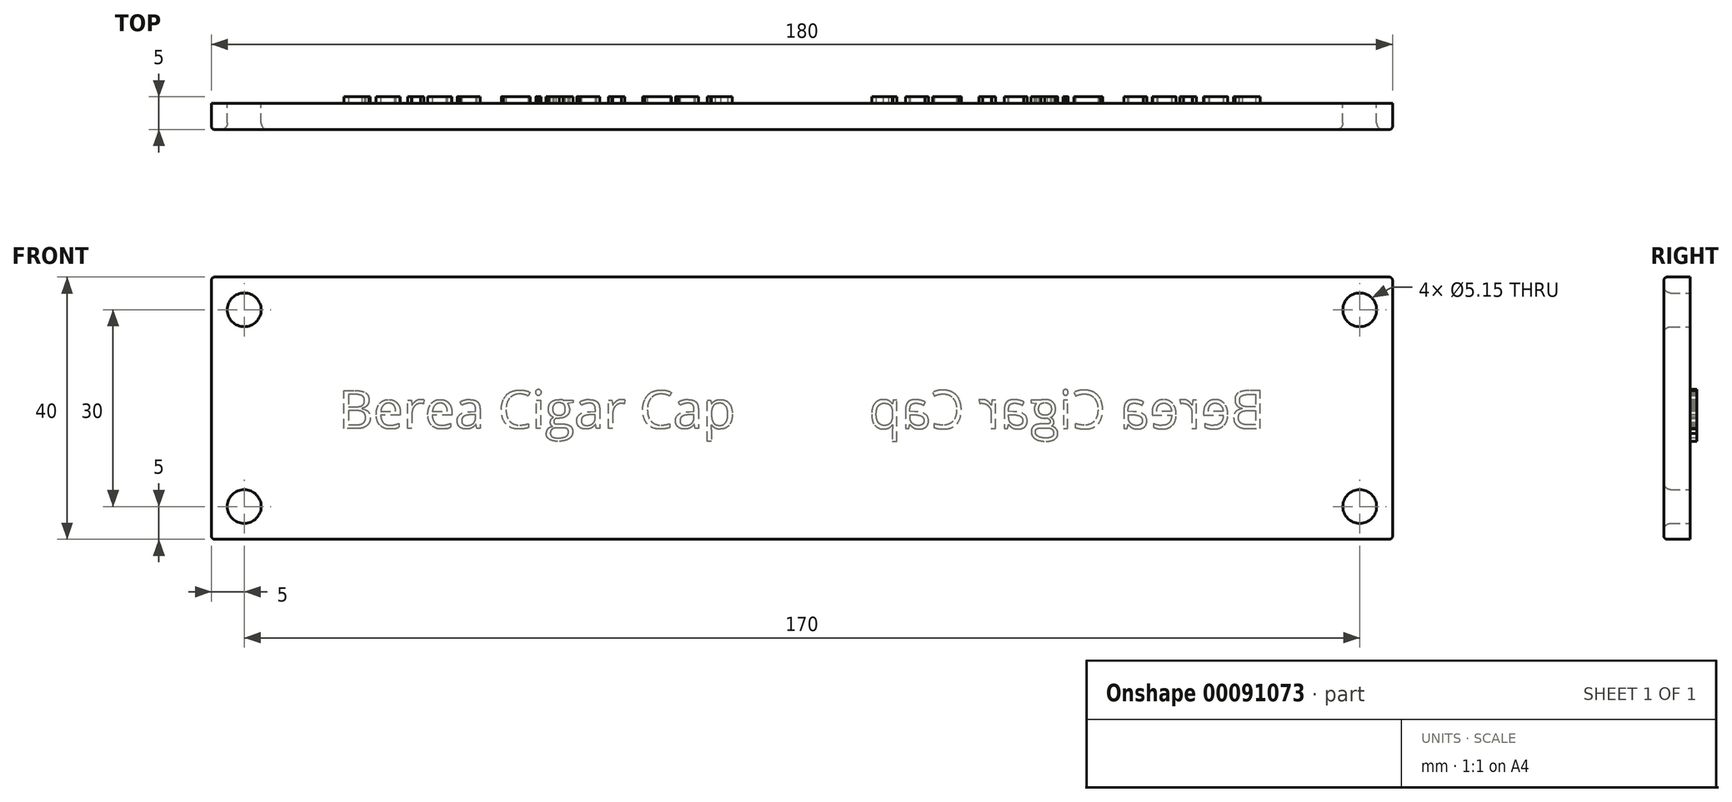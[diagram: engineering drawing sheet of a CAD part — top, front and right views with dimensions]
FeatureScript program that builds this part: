
annotation { "Feature Type Name" : "Feature", "Feature Type Description" : "" }
export const myFeature = defineFeature(function(context is Context, id is Id, definition is map)
    precondition{}
    {
        {
            var Q0;
            Q0=qCreatedBy(makeId("Front.planeOp"),FACE);
            var sketch = newSketch(context, id + "F0", { "sketchPlane" : qUnion([Q0])});
            skLineSegment(sketch, "E0.bottom", {"start": v(-90, -20) * mm, "end": v(90, -20) * mm});
            skLineSegment(sketch, "E0.top", {"start": v(-90, 20) * mm, "end": v(90, 20) * mm});
            skLineSegment(sketch, "E0.left", {"start": v(-90, -20) * mm, "end": v(-90, 20) * mm});
            skLineSegment(sketch, "E0.right", {"start": v(90, -20) * mm, "end": v(90, 20) * mm});
            skPoint(sketch, "E0.middle", {"position": v(0, 0) * mm});
            skCircle(sketch, "E1", {"center": v(-85, 15) * mm, "radius": 2.58 * mm});
            skPoint(sketch, "E2.start.orphan", {"position": v(-90, 0) * mm});
            skPoint(sketch, "E3.orphan", {"position": v(0, 20) * mm});
            skPoint(sketch, "E4.end.orphan", {"position": v(0, -20) * mm});
            skLineSegment(sketch, "E5", {"start": v(-90, 0) * mm, "end": v(0, 0) * mm, "construction": true});
            skLineSegment(sketch, "E6", {"start": v(0, 20) * mm, "end": v(0, -20) * mm, "construction": true});
            skCircle(sketch, "E7.MirrorC", {"center": v(-85, -15) * mm, "radius": 2.58 * mm});
            skCircle(sketch, "E8.MirrorC", {"center": v(85, 15) * mm, "radius": 2.58 * mm});
            skCircle(sketch, "E9.MirrorC", {"center": v(85, -15) * mm, "radius": 2.58 * mm});
            skSolve(sketch);
        }
        {
            var Q0;
            Q0=makeQuery(id+"F0.imprint","IMPRINT",FACE,{"disambiguationData":[TD([[makeQuery(id+"F0.imprint","IMPRINT",EDGE,{"derivedFrom":sQuery(id+"F0.wireOp",EDGE,"E0.bottom")}),1.0]])]});
            extrude(context, id + "F1", {"entities" : qUnion([Q0]), "depth" : 4 * mm});
        }
        {
            var Q0;
            Q0=makeQuery(id+"F1.opExtrude","CAP_EDGE",EDGE,{"disambiguationData":[OSD([sQuery(id+"F0.wireOp",EDGE,"E1")])],"isStart":false});
            var Q1;
            Q1=makeQuery(id+"F1.opExtrude","CAP_EDGE",EDGE,{"disambiguationData":[OSD([sQuery(id+"F0.wireOp",EDGE,"f5b72a5b-8583-449a-bdbf-9ac5a681e1fd0.MirrorC")])],"isStart":false});
            var Q2;
            Q2=makeQuery(id+"F1.opExtrude","CAP_EDGE",EDGE,{"disambiguationData":[OSD([sQuery(id+"F0.wireOp",EDGE,"2623e306-60f4-4522-aa65-1e3e8c2cf5b60.MirrorC")])],"isStart":false});
            var Q3;
            Q3=makeQuery(id+"F1.opExtrude","CAP_EDGE",EDGE,{"disambiguationData":[OSD([sQuery(id+"F0.wireOp",EDGE,"be81a34d-1d50-4ce7-a7a8-4484a1701fac0.MirrorC")])],"isStart":false});
            var Q4;
            Q4=makeQuery(id+"F1.opExtrude","CAP_EDGE",EDGE,{"disambiguationData":[OSD([sQuery(id+"F0.wireOp",EDGE,"E7.MirrorC")])],"isStart":false});
            var Q5;
            Q5=makeQuery(id+"F1.opExtrude","CAP_EDGE",EDGE,{"disambiguationData":[OSD([sQuery(id+"F0.wireOp",EDGE,"E8.MirrorC")])],"isStart":false});
            var Q6;
            Q6=makeQuery(id+"F1.opExtrude","CAP_EDGE",EDGE,{"disambiguationData":[OSD([sQuery(id+"F0.wireOp",EDGE,"E9.MirrorC")])],"isStart":false});
            fillet(context, id + "F2", {"entities" : qUnion([Q0, Q1, Q2, Q3, Q4, Q5, Q6]), "radius" : 1 * mm, "tangentPropagation" : true, "allowEdgeOverflow" : false});
        }
        {
            var Q0;
            Q0=makeQuery(id+"F1.opExtrude","CAP_EDGE",EDGE,{"disambiguationData":[OSD([sQuery(id+"F0.wireOp",EDGE,"E0.top")])],"isStart":false});
            var Q1;
            Q1=makeQuery(id+"F1.opExtrude","CAP_EDGE",EDGE,{"disambiguationData":[OSD([sQuery(id+"F0.wireOp",EDGE,"E0.left")])],"isStart":false});
            var Q2;
            Q2=makeQuery(id+"F1.opExtrude","CAP_EDGE",EDGE,{"disambiguationData":[OSD([sQuery(id+"F0.wireOp",EDGE,"E0.bottom")])],"isStart":false});
            var Q3;
            Q3=makeQuery(id+"F1.opExtrude","CAP_EDGE",EDGE,{"disambiguationData":[OSD([sQuery(id+"F0.wireOp",EDGE,"E0.right")])],"isStart":false});
            var Q4;
            Q4=makeQuery(id+"F1.opExtrude","SWEPT_EDGE",EDGE,{"disambiguationData":[OSD([sQuery(id+"F0.wireOp",EDGE,"E0.top"),sQuery(id+"F0.wireOp",EDGE,"E0.left")])]});
            var Q5;
            Q5=makeQuery(id+"F1.opExtrude","SWEPT_EDGE",EDGE,{"disambiguationData":[OSD([sQuery(id+"F0.wireOp",EDGE,"E0.bottom"),sQuery(id+"F0.wireOp",EDGE,"E0.left")])]});
            var Q6;
            Q6=makeQuery(id+"F1.opExtrude","SWEPT_EDGE",EDGE,{"disambiguationData":[OSD([sQuery(id+"F0.wireOp",EDGE,"E0.top"),sQuery(id+"F0.wireOp",EDGE,"E0.right")])]});
            var Q7;
            Q7=makeQuery(id+"F1.opExtrude","SWEPT_EDGE",EDGE,{"disambiguationData":[OSD([sQuery(id+"F0.wireOp",EDGE,"E0.bottom"),sQuery(id+"F0.wireOp",EDGE,"E0.right")])]});
            fillet(context, id + "F3", {"entities" : qUnion([Q0, Q1, Q2, Q3, Q4, Q5, Q6, Q7]), "radius" : .5 * mm, "tangentPropagation" : true, "allowEdgeOverflow" : false});
        }
        {
            var Q0;
            Q0=makeQuery(id+"F1.opExtrude","CAP_FACE",FACE,{"disambiguationData":[OSD([sQuery(id+"F0.wireOp",EDGE,"E0.bottom"),sQuery(id+"F0.wireOp",EDGE,"E0.top"),sQuery(id+"F0.wireOp",EDGE,"E0.left"),sQuery(id+"F0.wireOp",EDGE,"E0.right"),sQuery(id+"F0.wireOp",EDGE,"E1"),sQuery(id+"F0.wireOp",EDGE,"E7.MirrorC"),sQuery(id+"F0.wireOp",EDGE,"E8.MirrorC"),sQuery(id+"F0.wireOp",EDGE,"E9.MirrorC")])],"isStart":true});
            var sketch = newSketch(context, id + "F4", { "sketchPlane" : qUnion([Q0])});
            skText(sketch, "E10", { "text": "Berea Cigar Cap", "fontName": "OpenSans-Regular.ttf"});
            skLineSegment(sketch, "E11", {"start": v(0, 20) * mm, "end": v(0, -20) * mm, "construction": true});
            const initialGuessF4  = {"E10": [-0.0706, -0.0031, 1, 0, 0.00584]};
            skSetInitialGuess(sketch, initialGuessF4);
            skSolve(sketch);
        }
        {
            var Q0;
            Q0=qSketchRegion(id+"F4",true);
            extrude(context, id + "F5", {"entities" : qUnion([Q0]), "operationType" : NewBodyOperationType.ADD, "depth" : 1 * mm});
        }
        {
            var Q0;
            Q0=makeQuery(id+"F1.opExtrude","SWEPT_BODY",BODY,{"disambiguationData":[OSD([sQuery(id+"F0.wireOp",EDGE,"E0.bottom"),sQuery(id+"F0.wireOp",EDGE,"E0.top"),sQuery(id+"F0.wireOp",EDGE,"E0.left"),sQuery(id+"F0.wireOp",EDGE,"E0.right"),sQuery(id+"F0.wireOp",EDGE,"E1"),sQuery(id+"F0.wireOp",EDGE,"E7.MirrorC"),sQuery(id+"F0.wireOp",EDGE,"E8.MirrorC"),sQuery(id+"F0.wireOp",EDGE,"E9.MirrorC")])]});
            var Q1;
            Q1=makeQuery(id+"F5.opExtrude","SWEPT_FACE",FACE,{"disambiguationData":[OSD([sQuery(id+"F4.wireOp",EDGE,"E10.sketch_text.stroke-94")])]});
            var Q2;
            Q2=makeQuery(id+"F5.opExtrude","SWEPT_FACE",FACE,{"disambiguationData":[OSD([sQuery(id+"F4.wireOp",EDGE,"E10.sketch_text.stroke-169")])]});
            var Q3;
            Q3=makeQuery(id+"F5.opExtrude","SWEPT_FACE",FACE,{"disambiguationData":[OSD([sQuery(id+"F4.wireOp",EDGE,"E10.sketch_text.stroke-185")])]});
            var Q4;
            Q4=makeQuery(id+"F5.opExtrude","SWEPT_FACE",FACE,{"disambiguationData":[OSD([sQuery(id+"F4.wireOp",EDGE,"E10.sketch_text.stroke-125")])]});
            var Q5;
            Q5=makeQuery(id+"F5.opExtrude","SWEPT_FACE",FACE,{"disambiguationData":[OSD([sQuery(id+"F4.wireOp",EDGE,"E10.sketch_text.stroke-155")])]});
            var Q6;
            Q6=makeQuery(id+"F5.opExtrude","SWEPT_FACE",FACE,{"disambiguationData":[OSD([sQuery(id+"F4.wireOp",EDGE,"E10.sketch_text.stroke-65")])]});
            var Q7;
            Q7=makeQuery(id+"F5.opExtrude","SWEPT_FACE",FACE,{"disambiguationData":[OSD([sQuery(id+"F4.wireOp",EDGE,"E10.sketch_text.stroke-81")])]});
            var Q8;
            Q8=makeQuery(id+"F5.opExtrude","SWEPT_FACE",FACE,{"disambiguationData":[OSD([sQuery(id+"F4.wireOp",EDGE,"E10.sketch_text.stroke-67")])]});
            var Q9;
            Q9=makeQuery(id+"F5.opExtrude","SWEPT_FACE",FACE,{"disambiguationData":[OSD([sQuery(id+"F4.wireOp",EDGE,"E10.sketch_text.stroke-99")])]});
            var Q10;
            Q10=makeQuery(id+"F5.opExtrude","SWEPT_FACE",FACE,{"disambiguationData":[OSD([sQuery(id+"F4.wireOp",EDGE,"E10.sketch_text.stroke-127")])]});
            var Q11;
            Q11=makeQuery(id+"F5.opExtrude","SWEPT_FACE",FACE,{"disambiguationData":[OSD([sQuery(id+"F4.wireOp",EDGE,"E10.sketch_text.stroke-10")])]});
            var Q12;
            Q12=makeQuery(id+"F5.opExtrude","CAP_FACE",FACE,{"disambiguationData":[OSD([sQuery(id+"F4.wireOp",EDGE,"E10.sketch_text.stroke-9"),sQuery(id+"F4.wireOp",EDGE,"E10.sketch_text.stroke-10"),sQuery(id+"F4.wireOp",EDGE,"E10.sketch_text.stroke-11"),sQuery(id+"F4.wireOp",EDGE,"E10.sketch_text.stroke-12")])],"isStart":false});
            var Q13;
            Q13=makeQuery(id+"F5.opExtrude","SWEPT_FACE",FACE,{"disambiguationData":[OSD([sQuery(id+"F4.wireOp",EDGE,"E10.sketch_text.stroke-154")])]});
            var Q14;
            Q14=makeQuery(id+"F5.opExtrude","SWEPT_FACE",FACE,{"disambiguationData":[OSD([sQuery(id+"F4.wireOp",EDGE,"E10.sketch_text.stroke-1")])]});
            var Q15;
            Q15=makeQuery(id+"F5.opExtrude","CAP_FACE",FACE,{"disambiguationData":[OSD([sQuery(id+"F4.wireOp",EDGE,"E10.sketch_text.stroke-124"),sQuery(id+"F4.wireOp",EDGE,"E10.sketch_text.stroke-125"),sQuery(id+"F4.wireOp",EDGE,"E10.sketch_text.stroke-126"),sQuery(id+"F4.wireOp",EDGE,"E10.sketch_text.stroke-127"),sQuery(id+"F4.wireOp",EDGE,"E10.sketch_text.stroke-128"),sQuery(id+"F4.wireOp",EDGE,"E10.sketch_text.stroke-129"),sQuery(id+"F4.wireOp",EDGE,"E10.sketch_text.stroke-130"),sQuery(id+"F4.wireOp",EDGE,"E10.sketch_text.stroke-131"),sQuery(id+"F4.wireOp",EDGE,"E10.sketch_text.stroke-132"),sQuery(id+"F4.wireOp",EDGE,"E10.sketch_text.stroke-133"),sQuery(id+"F4.wireOp",EDGE,"E10.sketch_text.stroke-134"),sQuery(id+"F4.wireOp",EDGE,"E10.sketch_text.stroke-135"),sQuery(id+"F4.wireOp",EDGE,"E10.sketch_text.stroke-136"),sQuery(id+"F4.wireOp",EDGE,"E10.sketch_text.stroke-137"),sQuery(id+"F4.wireOp",EDGE,"E10.sketch_text.stroke-138")])],"isStart":false});
            var Q16;
            Q16=makeQuery(id+"F5.opExtrude","CAP_FACE",FACE,{"disambiguationData":[OSD([sQuery(id+"F4.wireOp",EDGE,"E10.sketch_text.stroke-34"),sQuery(id+"F4.wireOp",EDGE,"E10.sketch_text.stroke-35"),sQuery(id+"F4.wireOp",EDGE,"E10.sketch_text.stroke-36"),sQuery(id+"F4.wireOp",EDGE,"E10.sketch_text.stroke-37"),sQuery(id+"F4.wireOp",EDGE,"E10.sketch_text.stroke-38"),sQuery(id+"F4.wireOp",EDGE,"E10.sketch_text.stroke-39"),sQuery(id+"F4.wireOp",EDGE,"E10.sketch_text.stroke-40"),sQuery(id+"F4.wireOp",EDGE,"E10.sketch_text.stroke-41"),sQuery(id+"F4.wireOp",EDGE,"E10.sketch_text.stroke-42"),sQuery(id+"F4.wireOp",EDGE,"E10.sketch_text.stroke-43"),sQuery(id+"F4.wireOp",EDGE,"E10.sketch_text.stroke-44"),sQuery(id+"F4.wireOp",EDGE,"E10.sketch_text.stroke-45"),sQuery(id+"F4.wireOp",EDGE,"E10.sketch_text.stroke-46"),sQuery(id+"F4.wireOp",EDGE,"E10.sketch_text.stroke-47"),sQuery(id+"F4.wireOp",EDGE,"E10.sketch_text.stroke-48"),sQuery(id+"F4.wireOp",EDGE,"E10.sketch_text.stroke-49"),sQuery(id+"F4.wireOp",EDGE,"E10.sketch_text.stroke-50"),sQuery(id+"F4.wireOp",EDGE,"E10.sketch_text.stroke-51"),sQuery(id+"F4.wireOp",EDGE,"E10.sketch_text.stroke-52"),sQuery(id+"F4.wireOp",EDGE,"E10.sketch_text.stroke-53"),sQuery(id+"F4.wireOp",EDGE,"E10.sketch_text.stroke-54"),sQuery(id+"F4.wireOp",EDGE,"E10.sketch_text.stroke-55"),sQuery(id+"F4.wireOp",EDGE,"E10.sketch_text.stroke-56"),sQuery(id+"F4.wireOp",EDGE,"E10.sketch_text.stroke-57"),sQuery(id+"F4.wireOp",EDGE,"E10.sketch_text.stroke-58"),sQuery(id+"F4.wireOp",EDGE,"E10.sketch_text.stroke-59"),sQuery(id+"F4.wireOp",EDGE,"E10.sketch_text.stroke-60")])],"isStart":false});
            var Q17;
            Q17=makeQuery(id+"F5.opExtrude","SWEPT_FACE",FACE,{"disambiguationData":[OSD([sQuery(id+"F4.wireOp",EDGE,"E10.sketch_text.stroke-50")])]});
            var Q18;
            Q18=makeQuery(id+"F5.opExtrude","SWEPT_FACE",FACE,{"disambiguationData":[OSD([sQuery(id+"F4.wireOp",EDGE,"E10.sketch_text.stroke-2")])]});
            var Q19;
            Q19=makeQuery(id+"F5.opExtrude","SWEPT_FACE",FACE,{"disambiguationData":[OSD([sQuery(id+"F4.wireOp",EDGE,"E10.sketch_text.stroke-3")])]});
            var Q20;
            Q20=makeQuery(id+"F5.opExtrude","SWEPT_FACE",FACE,{"disambiguationData":[OSD([sQuery(id+"F4.wireOp",EDGE,"E10.sketch_text.stroke-5")])]});
            var Q21;
            Q21=makeQuery(id+"F5.opExtrude","SWEPT_FACE",FACE,{"disambiguationData":[OSD([sQuery(id+"F4.wireOp",EDGE,"E10.sketch_text.stroke-8")])]});
            var Q22;
            Q22=makeQuery(id+"F5.opExtrude","SWEPT_FACE",FACE,{"disambiguationData":[OSD([sQuery(id+"F4.wireOp",EDGE,"E10.sketch_text.stroke-98")])]});
            var Q23;
            Q23=makeQuery(id+"F5.opExtrude","SWEPT_FACE",FACE,{"disambiguationData":[OSD([sQuery(id+"F4.wireOp",EDGE,"E10.sketch_text.stroke-66")])]});
            var Q24;
            Q24=makeQuery(id+"F5.opExtrude","SWEPT_FACE",FACE,{"disambiguationData":[OSD([sQuery(id+"F4.wireOp",EDGE,"E10.sketch_text.stroke-153")])]});
            var Q25;
            Q25=makeQuery(id+"F5.opExtrude","SWEPT_FACE",FACE,{"disambiguationData":[OSD([sQuery(id+"F4.wireOp",EDGE,"E10.sketch_text.stroke-126")])]});
            var Q26;
            Q26=makeQuery(id+"F5.opExtrude","SWEPT_FACE",FACE,{"disambiguationData":[OSD([sQuery(id+"F4.wireOp",EDGE,"E10.sketch_text.stroke-183")])]});
            var Q27;
            Q27=makeQuery(id+"F5.opExtrude","SWEPT_FACE",FACE,{"disambiguationData":[OSD([sQuery(id+"F4.wireOp",EDGE,"E10.sketch_text.stroke-109")])]});
            var Q28;
            Q28=makeQuery(id+"F5.opExtrude","SWEPT_FACE",FACE,{"disambiguationData":[OSD([sQuery(id+"F4.wireOp",EDGE,"E10.sketch_text.stroke-186")])]});
            var Q29;
            Q29=makeQuery(id+"F5.opExtrude","SWEPT_FACE",FACE,{"disambiguationData":[OSD([sQuery(id+"F4.wireOp",EDGE,"E10.sketch_text.stroke-79")])]});
            var Q30;
            Q30=makeQuery(id+"F5.opExtrude","SWEPT_FACE",FACE,{"disambiguationData":[OSD([sQuery(id+"F4.wireOp",EDGE,"E10.sketch_text.stroke-110")])]});
            var Q31;
            Q31=makeQuery(id+"F5.opExtrude","SWEPT_FACE",FACE,{"disambiguationData":[OSD([sQuery(id+"F4.wireOp",EDGE,"E10.sketch_text.stroke-38")])]});
            var Q32;
            Q32=makeQuery(id+"F5.opExtrude","SWEPT_FACE",FACE,{"disambiguationData":[OSD([sQuery(id+"F4.wireOp",EDGE,"E10.sketch_text.stroke-24")])]});
            var Q33;
            Q33=makeQuery(id+"F5.opExtrude","SWEPT_FACE",FACE,{"disambiguationData":[OSD([sQuery(id+"F4.wireOp",EDGE,"E10.sketch_text.stroke-12")])]});
            var Q34;
            Q34=makeQuery(id+"F5.opExtrude","SWEPT_FACE",FACE,{"disambiguationData":[OSD([sQuery(id+"F4.wireOp",EDGE,"E10.sketch_text.stroke-100")])]});
            var Q35;
            Q35=makeQuery(id+"F5.opExtrude","SWEPT_FACE",FACE,{"disambiguationData":[OSD([sQuery(id+"F4.wireOp",EDGE,"E10.sketch_text.stroke-158")])]});
            var Q36;
            Q36=makeQuery(id+"F5.opExtrude","SWEPT_FACE",FACE,{"disambiguationData":[OSD([sQuery(id+"F4.wireOp",EDGE,"E10.sketch_text.stroke-142")])]});
            var Q37;
            Q37=makeQuery(id+"F5.opExtrude","SWEPT_FACE",FACE,{"disambiguationData":[OSD([sQuery(id+"F4.wireOp",EDGE,"E10.sketch_text.stroke-54")])]});
            var Q38;
            Q38=makeQuery(id+"F5.opExtrude","SWEPT_FACE",FACE,{"disambiguationData":[OSD([sQuery(id+"F4.wireOp",EDGE,"E10.sketch_text.stroke-25")])]});
            var Q39;
            Q39=makeQuery(id+"F5.opExtrude","SWEPT_FACE",FACE,{"disambiguationData":[OSD([sQuery(id+"F4.wireOp",EDGE,"E10.sketch_text.stroke-101")])]});
            var Q40;
            Q40=makeQuery(id+"F5.opExtrude","SWEPT_FACE",FACE,{"disambiguationData":[OSD([sQuery(id+"F4.wireOp",EDGE,"E10.sketch_text.stroke-69")])]});
            var Q41;
            Q41=makeQuery(id+"F5.opExtrude","SWEPT_FACE",FACE,{"disambiguationData":[OSD([sQuery(id+"F4.wireOp",EDGE,"E10.sketch_text.stroke-159")])]});
            var Q42;
            Q42=makeQuery(id+"F5.opExtrude","SWEPT_FACE",FACE,{"disambiguationData":[OSD([sQuery(id+"F4.wireOp",EDGE,"E10.sketch_text.stroke-85")])]});
            var Q43;
            Q43=makeQuery(id+"F5.opExtrude","SWEPT_FACE",FACE,{"disambiguationData":[OSD([sQuery(id+"F4.wireOp",EDGE,"E10.sketch_text.stroke-173")])]});
            var Q44;
            Q44=makeQuery(id+"F5.opExtrude","SWEPT_FACE",FACE,{"disambiguationData":[OSD([sQuery(id+"F4.wireOp",EDGE,"E10.sketch_text.stroke-40")])]});
            var Q45;
            Q45=makeQuery(id+"F5.opExtrude","SWEPT_FACE",FACE,{"disambiguationData":[OSD([sQuery(id+"F4.wireOp",EDGE,"E10.sketch_text.stroke-102")])]});
            var Q46;
            Q46=makeQuery(id+"F5.opExtrude","SWEPT_FACE",FACE,{"disambiguationData":[OSD([sQuery(id+"F4.wireOp",EDGE,"E10.sketch_text.stroke-86")])]});
            var Q47;
            Q47=makeQuery(id+"F5.opExtrude","SWEPT_FACE",FACE,{"disambiguationData":[OSD([sQuery(id+"F4.wireOp",EDGE,"E10.sketch_text.stroke-130")])]});
            var Q48;
            Q48=makeQuery(id+"F5.opExtrude","SWEPT_FACE",FACE,{"disambiguationData":[OSD([sQuery(id+"F4.wireOp",EDGE,"E10.sketch_text.stroke-103")])]});
            var Q49;
            Q49=makeQuery(id+"F5.opExtrude","SWEPT_FACE",FACE,{"disambiguationData":[OSD([sQuery(id+"F4.wireOp",EDGE,"E10.sketch_text.stroke-87")])]});
            var Q50;
            Q50=makeQuery(id+"F5.opExtrude","SWEPT_FACE",FACE,{"disambiguationData":[OSD([sQuery(id+"F4.wireOp",EDGE,"E10.sketch_text.stroke-145")])]});
            var Q51;
            Q51=makeQuery(id+"F5.opExtrude","SWEPT_FACE",FACE,{"disambiguationData":[OSD([sQuery(id+"F4.wireOp",EDGE,"E10.sketch_text.stroke-131")])]});
            var Q52;
            Q52=makeQuery(id+"F5.opExtrude","SWEPT_FACE",FACE,{"disambiguationData":[OSD([sQuery(id+"F4.wireOp",EDGE,"E10.sketch_text.stroke-28")])]});
            var Q53;
            Q53=makeQuery(id+"F5.opExtrude","SWEPT_FACE",FACE,{"disambiguationData":[OSD([sQuery(id+"F4.wireOp",EDGE,"E10.sketch_text.stroke-14")])]});
            var Q54;
            Q54=makeQuery(id+"F5.opExtrude","SWEPT_FACE",FACE,{"disambiguationData":[OSD([sQuery(id+"F4.wireOp",EDGE,"E10.sketch_text.stroke-88")])]});
            var Q55;
            Q55=makeQuery(id+"F5.opExtrude","SWEPT_FACE",FACE,{"disambiguationData":[OSD([sQuery(id+"F4.wireOp",EDGE,"E10.sketch_text.stroke-162")])]});
            var Q56;
            Q56=makeQuery(id+"F5.opExtrude","SWEPT_FACE",FACE,{"disambiguationData":[OSD([sQuery(id+"F4.wireOp",EDGE,"E10.sketch_text.stroke-176")])]});
            var Q57;
            Q57=makeQuery(id+"F5.opExtrude","SWEPT_FACE",FACE,{"disambiguationData":[OSD([sQuery(id+"F4.wireOp",EDGE,"E10.sketch_text.stroke-73")])]});
            var Q58;
            Q58=makeQuery(id+"F5.opExtrude","SWEPT_FACE",FACE,{"disambiguationData":[OSD([sQuery(id+"F4.wireOp",EDGE,"E10.sketch_text.stroke-59")])]});
            var Q59;
            Q59=makeQuery(id+"F5.opExtrude","SWEPT_FACE",FACE,{"disambiguationData":[OSD([sQuery(id+"F4.wireOp",EDGE,"E10.sketch_text.stroke-133")])]});
            var Q60;
            Q60=makeQuery(id+"F5.opExtrude","SWEPT_FACE",FACE,{"disambiguationData":[OSD([sQuery(id+"F4.wireOp",EDGE,"E10.sketch_text.stroke-119")])]});
            var Q61;
            Q61=makeQuery(id+"F5.opExtrude","SWEPT_FACE",FACE,{"disambiguationData":[OSD([sQuery(id+"F4.wireOp",EDGE,"E10.sketch_text.stroke-74")])]});
            var Q62;
            Q62=makeQuery(id+"F5.opExtrude","SWEPT_FACE",FACE,{"disambiguationData":[OSD([sQuery(id+"F4.wireOp",EDGE,"E10.sketch_text.stroke-44")])]});
            var Q63;
            Q63=makeQuery(id+"F5.opExtrude","SWEPT_FACE",FACE,{"disambiguationData":[OSD([sQuery(id+"F4.wireOp",EDGE,"E10.sketch_text.stroke-120")])]});
            var Q64;
            Q64=makeQuery(id+"F5.opExtrude","SWEPT_FACE",FACE,{"disambiguationData":[OSD([sQuery(id+"F4.wireOp",EDGE,"E10.sketch_text.stroke-90")])]});
            var Q65;
            Q65=makeQuery(id+"F5.opExtrude","SWEPT_FACE",FACE,{"disambiguationData":[OSD([sQuery(id+"F4.wireOp",EDGE,"E10.sketch_text.stroke-178")])]});
            var Q66;
            Q66=makeQuery(id+"F5.opExtrude","SWEPT_FACE",FACE,{"disambiguationData":[OSD([sQuery(id+"F4.wireOp",EDGE,"E10.sketch_text.stroke-45")])]});
            var Q67;
            Q67=makeQuery(id+"F5.opExtrude","SWEPT_FACE",FACE,{"disambiguationData":[OSD([sQuery(id+"F4.wireOp",EDGE,"E10.sketch_text.stroke-31")])]});
            var Q68;
            Q68=makeQuery(id+"F5.opExtrude","SWEPT_FACE",FACE,{"disambiguationData":[OSD([sQuery(id+"F4.wireOp",EDGE,"E10.sketch_text.stroke-135")])]});
            var Q69;
            Q69=makeQuery(id+"F5.opExtrude","SWEPT_FACE",FACE,{"disambiguationData":[OSD([sQuery(id+"F4.wireOp",EDGE,"E10.sketch_text.stroke-179")])]});
            var Q70;
            Q70=makeQuery(id+"F5.opExtrude","SWEPT_FACE",FACE,{"disambiguationData":[OSD([sQuery(id+"F4.wireOp",EDGE,"E10.sketch_text.stroke-165")])]});
            var Q71;
            Q71=makeQuery(id+"F5.opExtrude","SWEPT_FACE",FACE,{"disambiguationData":[OSD([sQuery(id+"F4.wireOp",EDGE,"E10.sketch_text.stroke-149")])]});
            var Q72;
            Q72=makeQuery(id+"F5.opExtrude","SWEPT_FACE",FACE,{"disambiguationData":[OSD([sQuery(id+"F4.wireOp",EDGE,"E10.sketch_text.stroke-136")])]});
            var Q73;
            Q73=makeQuery(id+"F5.opExtrude","SWEPT_FACE",FACE,{"disambiguationData":[OSD([sQuery(id+"F4.wireOp",EDGE,"E10.sketch_text.stroke-122")])]});
            var Q74;
            Q74=makeQuery(id+"F5.opExtrude","SWEPT_FACE",FACE,{"disambiguationData":[OSD([sQuery(id+"F4.wireOp",EDGE,"E10.sketch_text.stroke-106")])]});
            var Q75;
            Q75=makeQuery(id+"F5.opExtrude","SWEPT_FACE",FACE,{"disambiguationData":[OSD([sQuery(id+"F4.wireOp",EDGE,"E10.sketch_text.stroke-180")])]});
            var Q76;
            Q76=makeQuery(id+"F5.opExtrude","SWEPT_FACE",FACE,{"disambiguationData":[OSD([sQuery(id+"F4.wireOp",EDGE,"E10.sketch_text.stroke-166")])]});
            var Q77;
            Q77=makeQuery(id+"F5.opExtrude","SWEPT_FACE",FACE,{"disambiguationData":[OSD([sQuery(id+"F4.wireOp",EDGE,"E10.sketch_text.stroke-150")])]});
            var Q78;
            Q78=makeQuery(id+"F5.opExtrude","SWEPT_FACE",FACE,{"disambiguationData":[OSD([sQuery(id+"F4.wireOp",EDGE,"E10.sketch_text.stroke-76")])]});
            var Q79;
            Q79=makeQuery(id+"F5.opExtrude","SWEPT_FACE",FACE,{"disambiguationData":[OSD([sQuery(id+"F4.wireOp",EDGE,"E10.sketch_text.stroke-32")])]});
            var Q80;
            Q80=makeQuery(id+"F5.opExtrude","SWEPT_FACE",FACE,{"disambiguationData":[OSD([sQuery(id+"F4.wireOp",EDGE,"E10.sketch_text.stroke-181")])]});
            var Q81;
            Q81=makeQuery(id+"F5.opExtrude","SWEPT_FACE",FACE,{"disambiguationData":[OSD([sQuery(id+"F4.wireOp",EDGE,"E10.sketch_text.stroke-47")])]});
            var Q82;
            Q82=makeQuery(id+"F5.opExtrude","SWEPT_FACE",FACE,{"disambiguationData":[OSD([sQuery(id+"F4.wireOp",EDGE,"E10.sketch_text.stroke-123")])]});
            var Q83;
            Q83=makeQuery(id+"F5.opExtrude","SWEPT_FACE",FACE,{"disambiguationData":[OSD([sQuery(id+"F4.wireOp",EDGE,"E10.sketch_text.stroke-107")])]});
            var Q84;
            Q84=makeQuery(id+"F5.opExtrude","SWEPT_FACE",FACE,{"disambiguationData":[OSD([sQuery(id+"F4.wireOp",EDGE,"E10.sketch_text.stroke-48")])]});
            var Q85;
            Q85=makeQuery(id+"F5.opExtrude","SWEPT_FACE",FACE,{"disambiguationData":[OSD([sQuery(id+"F4.wireOp",EDGE,"E10.sketch_text.stroke-124")])]});
            var Q86;
            Q86=makeQuery(id+"F5.opExtrude","SWEPT_FACE",FACE,{"disambiguationData":[OSD([sQuery(id+"F4.wireOp",EDGE,"E10.sketch_text.stroke-108")])]});
            var Q87;
            Q87=makeQuery(id+"F5.opExtrude","CAP_FACE",FACE,{"disambiguationData":[OSD([sQuery(id+"F4.wireOp",EDGE,"E10.sketch_text.stroke-139"),sQuery(id+"F4.wireOp",EDGE,"E10.sketch_text.stroke-140"),sQuery(id+"F4.wireOp",EDGE,"E10.sketch_text.stroke-141"),sQuery(id+"F4.wireOp",EDGE,"E10.sketch_text.stroke-142"),sQuery(id+"F4.wireOp",EDGE,"E10.sketch_text.stroke-143"),sQuery(id+"F4.wireOp",EDGE,"E10.sketch_text.stroke-144"),sQuery(id+"F4.wireOp",EDGE,"E10.sketch_text.stroke-145"),sQuery(id+"F4.wireOp",EDGE,"E10.sketch_text.stroke-146"),sQuery(id+"F4.wireOp",EDGE,"E10.sketch_text.stroke-147"),sQuery(id+"F4.wireOp",EDGE,"E10.sketch_text.stroke-148"),sQuery(id+"F4.wireOp",EDGE,"E10.sketch_text.stroke-149"),sQuery(id+"F4.wireOp",EDGE,"E10.sketch_text.stroke-150"),sQuery(id+"F4.wireOp",EDGE,"E10.sketch_text.stroke-151"),sQuery(id+"F4.wireOp",EDGE,"E10.sketch_text.stroke-152"),sQuery(id+"F4.wireOp",EDGE,"E10.sketch_text.stroke-153"),sQuery(id+"F4.wireOp",EDGE,"E10.sketch_text.stroke-154"),sQuery(id+"F4.wireOp",EDGE,"E10.sketch_text.stroke-155"),sQuery(id+"F4.wireOp",EDGE,"E10.sketch_text.stroke-156"),sQuery(id+"F4.wireOp",EDGE,"E10.sketch_text.stroke-157"),sQuery(id+"F4.wireOp",EDGE,"E10.sketch_text.stroke-158"),sQuery(id+"F4.wireOp",EDGE,"E10.sketch_text.stroke-159"),sQuery(id+"F4.wireOp",EDGE,"E10.sketch_text.stroke-160"),sQuery(id+"F4.wireOp",EDGE,"E10.sketch_text.stroke-161"),sQuery(id+"F4.wireOp",EDGE,"E10.sketch_text.stroke-162"),sQuery(id+"F4.wireOp",EDGE,"E10.sketch_text.stroke-163"),sQuery(id+"F4.wireOp",EDGE,"E10.sketch_text.stroke-164"),sQuery(id+"F4.wireOp",EDGE,"E10.sketch_text.stroke-165")])],"isStart":false});
            var Q88;
            Q88=makeQuery(id+"F5.opExtrude","CAP_FACE",FACE,{"disambiguationData":[OSD([sQuery(id+"F4.wireOp",EDGE,"E10.sketch_text.stroke-21"),sQuery(id+"F4.wireOp",EDGE,"E10.sketch_text.stroke-22"),sQuery(id+"F4.wireOp",EDGE,"E10.sketch_text.stroke-23"),sQuery(id+"F4.wireOp",EDGE,"E10.sketch_text.stroke-24"),sQuery(id+"F4.wireOp",EDGE,"E10.sketch_text.stroke-25"),sQuery(id+"F4.wireOp",EDGE,"E10.sketch_text.stroke-26"),sQuery(id+"F4.wireOp",EDGE,"E10.sketch_text.stroke-27"),sQuery(id+"F4.wireOp",EDGE,"E10.sketch_text.stroke-28"),sQuery(id+"F4.wireOp",EDGE,"E10.sketch_text.stroke-29"),sQuery(id+"F4.wireOp",EDGE,"E10.sketch_text.stroke-30"),sQuery(id+"F4.wireOp",EDGE,"E10.sketch_text.stroke-31"),sQuery(id+"F4.wireOp",EDGE,"E10.sketch_text.stroke-32"),sQuery(id+"F4.wireOp",EDGE,"E10.sketch_text.stroke-33")])],"isStart":false});
            var Q89;
            Q89=makeQuery(id+"F5.opExtrude","SWEPT_FACE",FACE,{"disambiguationData":[OSD([sQuery(id+"F4.wireOp",EDGE,"E10.sketch_text.stroke-113")])]});
            var Q90;
            Q90=makeQuery(id+"F5.opExtrude","SWEPT_FACE",FACE,{"disambiguationData":[OSD([sQuery(id+"F4.wireOp",EDGE,"E10.sketch_text.stroke-37")])]});
            var Q91;
            Q91=makeQuery(id+"F5.opExtrude","SWEPT_FACE",FACE,{"disambiguationData":[OSD([sQuery(id+"F4.wireOp",EDGE,"E10.sketch_text.stroke-187")])]});
            var Q92;
            Q92=makeQuery(id+"F5.opExtrude","SWEPT_FACE",FACE,{"disambiguationData":[OSD([sQuery(id+"F4.wireOp",EDGE,"E10.sketch_text.stroke-0")])]});
            var Q93;
            Q93=makeQuery(id+"F5.opExtrude","SWEPT_FACE",FACE,{"disambiguationData":[OSD([sQuery(id+"F4.wireOp",EDGE,"E10.sketch_text.stroke-4")])]});
            var Q94;
            Q94=makeQuery(id+"F5.opExtrude","SWEPT_FACE",FACE,{"disambiguationData":[OSD([sQuery(id+"F4.wireOp",EDGE,"E10.sketch_text.stroke-82")])]});
            var Q95;
            Q95=makeQuery(id+"F5.opExtrude","SWEPT_FACE",FACE,{"disambiguationData":[OSD([sQuery(id+"F4.wireOp",EDGE,"E10.sketch_text.stroke-52")])]});
            var Q96;
            Q96=makeQuery(id+"F5.opExtrude","SWEPT_FACE",FACE,{"disambiguationData":[OSD([sQuery(id+"F4.wireOp",EDGE,"E10.sketch_text.stroke-49")])]});
            var Q97;
            Q97=makeQuery(id+"F5.opExtrude","SWEPT_FACE",FACE,{"disambiguationData":[OSD([sQuery(id+"F4.wireOp",EDGE,"E10.sketch_text.stroke-63")])]});
            var Q98;
            Q98=makeQuery(id+"F5.opExtrude","SWEPT_FACE",FACE,{"disambiguationData":[OSD([sQuery(id+"F4.wireOp",EDGE,"E10.sketch_text.stroke-21")])]});
            var Q99;
            Q99=makeQuery(id+"F5.opExtrude","SWEPT_FACE",FACE,{"disambiguationData":[OSD([sQuery(id+"F4.wireOp",EDGE,"E10.sketch_text.stroke-128")])]});
            var Q100;
            Q100=makeQuery(id+"F5.opExtrude","SWEPT_FACE",FACE,{"disambiguationData":[OSD([sQuery(id+"F4.wireOp",EDGE,"E10.sketch_text.stroke-55")])]});
            var Q101;
            Q101=makeQuery(id+"F5.opExtrude","SWEPT_FACE",FACE,{"disambiguationData":[OSD([sQuery(id+"F4.wireOp",EDGE,"E10.sketch_text.stroke-26")])]});
            var Q102;
            Q102=makeQuery(id+"F5.opExtrude","SWEPT_FACE",FACE,{"disambiguationData":[OSD([sQuery(id+"F4.wireOp",EDGE,"E10.sketch_text.stroke-174")])]});
            var Q103;
            Q103=makeQuery(id+"F5.opExtrude","SWEPT_FACE",FACE,{"disambiguationData":[OSD([sQuery(id+"F4.wireOp",EDGE,"E10.sketch_text.stroke-104")])]});
            var Q104;
            Q104=makeQuery(id+"F5.opExtrude","SWEPT_FACE",FACE,{"disambiguationData":[OSD([sQuery(id+"F4.wireOp",EDGE,"E10.sketch_text.stroke-72")])]});
            var Q105;
            Q105=makeQuery(id+"F5.opExtrude","SWEPT_FACE",FACE,{"disambiguationData":[OSD([sQuery(id+"F4.wireOp",EDGE,"E10.sketch_text.stroke-132")])]});
            var Q106;
            Q106=makeQuery(id+"F5.opExtrude","SWEPT_FACE",FACE,{"disambiguationData":[OSD([sQuery(id+"F4.wireOp",EDGE,"E10.sketch_text.stroke-43")])]});
            var Q107;
            Q107=makeQuery(id+"F5.opExtrude","SWEPT_FACE",FACE,{"disambiguationData":[OSD([sQuery(id+"F4.wireOp",EDGE,"E10.sketch_text.stroke-15")])]});
            var Q108;
            Q108=makeQuery(id+"F5.opExtrude","SWEPT_FACE",FACE,{"disambiguationData":[OSD([sQuery(id+"F4.wireOp",EDGE,"E10.sketch_text.stroke-89")])]});
            var Q109;
            Q109=makeQuery(id+"F5.opExtrude","SWEPT_FACE",FACE,{"disambiguationData":[OSD([sQuery(id+"F4.wireOp",EDGE,"E10.sketch_text.stroke-163")])]});
            var Q110;
            Q110=makeQuery(id+"F5.opExtrude","SWEPT_FACE",FACE,{"disambiguationData":[OSD([sQuery(id+"F4.wireOp",EDGE,"E10.sketch_text.stroke-30")])]});
            var Q111;
            Q111=makeQuery(id+"F5.opExtrude","SWEPT_FACE",FACE,{"disambiguationData":[OSD([sQuery(id+"F4.wireOp",EDGE,"E10.sketch_text.stroke-134")])]});
            var Q112;
            Q112=makeQuery(id+"F5.opExtrude","SWEPT_FACE",FACE,{"disambiguationData":[OSD([sQuery(id+"F4.wireOp",EDGE,"E10.sketch_text.stroke-121")])]});
            var Q113;
            Q113=makeQuery(id+"F5.opExtrude","CAP_FACE",FACE,{"disambiguationData":[OSD([sQuery(id+"F4.wireOp",EDGE,"E10.sketch_text.stroke-105"),sQuery(id+"F4.wireOp",EDGE,"E10.sketch_text.stroke-106"),sQuery(id+"F4.wireOp",EDGE,"E10.sketch_text.stroke-107"),sQuery(id+"F4.wireOp",EDGE,"E10.sketch_text.stroke-108"),sQuery(id+"F4.wireOp",EDGE,"E10.sketch_text.stroke-109"),sQuery(id+"F4.wireOp",EDGE,"E10.sketch_text.stroke-110"),sQuery(id+"F4.wireOp",EDGE,"E10.sketch_text.stroke-111"),sQuery(id+"F4.wireOp",EDGE,"E10.sketch_text.stroke-112"),sQuery(id+"F4.wireOp",EDGE,"E10.sketch_text.stroke-113"),sQuery(id+"F4.wireOp",EDGE,"E10.sketch_text.stroke-114"),sQuery(id+"F4.wireOp",EDGE,"E10.sketch_text.stroke-115"),sQuery(id+"F4.wireOp",EDGE,"E10.sketch_text.stroke-116"),sQuery(id+"F4.wireOp",EDGE,"E10.sketch_text.stroke-117"),sQuery(id+"F4.wireOp",EDGE,"E10.sketch_text.stroke-118"),sQuery(id+"F4.wireOp",EDGE,"E10.sketch_text.stroke-119"),sQuery(id+"F4.wireOp",EDGE,"E10.sketch_text.stroke-120"),sQuery(id+"F4.wireOp",EDGE,"E10.sketch_text.stroke-121"),sQuery(id+"F4.wireOp",EDGE,"E10.sketch_text.stroke-122"),sQuery(id+"F4.wireOp",EDGE,"E10.sketch_text.stroke-123")])],"isStart":false});
            var Q114;
            Q114=makeQuery(id+"F5.opExtrude","SWEPT_FACE",FACE,{"disambiguationData":[OSD([sQuery(id+"F4.wireOp",EDGE,"E10.sketch_text.stroke-92")])]});
            var Q115;
            Q115=makeQuery(id+"F5.opExtrude","SWEPT_FACE",FACE,{"disambiguationData":[OSD([sQuery(id+"F4.wireOp",EDGE,"E10.sketch_text.stroke-46")])]});
            var Q116;
            Q116=makeQuery(id+"F5.opExtrude","CAP_FACE",FACE,{"disambiguationData":[OSD([sQuery(id+"F4.wireOp",EDGE,"E10.sketch_text.stroke-61"),sQuery(id+"F4.wireOp",EDGE,"E10.sketch_text.stroke-62"),sQuery(id+"F4.wireOp",EDGE,"E10.sketch_text.stroke-63"),sQuery(id+"F4.wireOp",EDGE,"E10.sketch_text.stroke-64"),sQuery(id+"F4.wireOp",EDGE,"E10.sketch_text.stroke-65"),sQuery(id+"F4.wireOp",EDGE,"E10.sketch_text.stroke-66"),sQuery(id+"F4.wireOp",EDGE,"E10.sketch_text.stroke-67"),sQuery(id+"F4.wireOp",EDGE,"E10.sketch_text.stroke-68"),sQuery(id+"F4.wireOp",EDGE,"E10.sketch_text.stroke-69"),sQuery(id+"F4.wireOp",EDGE,"E10.sketch_text.stroke-70"),sQuery(id+"F4.wireOp",EDGE,"E10.sketch_text.stroke-71"),sQuery(id+"F4.wireOp",EDGE,"E10.sketch_text.stroke-72"),sQuery(id+"F4.wireOp",EDGE,"E10.sketch_text.stroke-73"),sQuery(id+"F4.wireOp",EDGE,"E10.sketch_text.stroke-74"),sQuery(id+"F4.wireOp",EDGE,"E10.sketch_text.stroke-75"),sQuery(id+"F4.wireOp",EDGE,"E10.sketch_text.stroke-76"),sQuery(id+"F4.wireOp",EDGE,"E10.sketch_text.stroke-77"),sQuery(id+"F4.wireOp",EDGE,"E10.sketch_text.stroke-78"),sQuery(id+"F4.wireOp",EDGE,"E10.sketch_text.stroke-79"),sQuery(id+"F4.wireOp",EDGE,"E10.sketch_text.stroke-80"),sQuery(id+"F4.wireOp",EDGE,"E10.sketch_text.stroke-81"),sQuery(id+"F4.wireOp",EDGE,"E10.sketch_text.stroke-82"),sQuery(id+"F4.wireOp",EDGE,"E10.sketch_text.stroke-83"),sQuery(id+"F4.wireOp",EDGE,"E10.sketch_text.stroke-84"),sQuery(id+"F4.wireOp",EDGE,"E10.sketch_text.stroke-85"),sQuery(id+"F4.wireOp",EDGE,"E10.sketch_text.stroke-86"),sQuery(id+"F4.wireOp",EDGE,"E10.sketch_text.stroke-87"),sQuery(id+"F4.wireOp",EDGE,"E10.sketch_text.stroke-88"),sQuery(id+"F4.wireOp",EDGE,"E10.sketch_text.stroke-89"),sQuery(id+"F4.wireOp",EDGE,"E10.sketch_text.stroke-90"),sQuery(id+"F4.wireOp",EDGE,"E10.sketch_text.stroke-91"),sQuery(id+"F4.wireOp",EDGE,"E10.sketch_text.stroke-92"),sQuery(id+"F4.wireOp",EDGE,"E10.sketch_text.stroke-93"),sQuery(id+"F4.wireOp",EDGE,"E10.sketch_text.stroke-94"),sQuery(id+"F4.wireOp",EDGE,"E10.sketch_text.stroke-95"),sQuery(id+"F4.wireOp",EDGE,"E10.sketch_text.stroke-96"),sQuery(id+"F4.wireOp",EDGE,"E10.sketch_text.stroke-97"),sQuery(id+"F4.wireOp",EDGE,"E10.sketch_text.stroke-98"),sQuery(id+"F4.wireOp",EDGE,"E10.sketch_text.stroke-99"),sQuery(id+"F4.wireOp",EDGE,"E10.sketch_text.stroke-100"),sQuery(id+"F4.wireOp",EDGE,"E10.sketch_text.stroke-101"),sQuery(id+"F4.wireOp",EDGE,"E10.sketch_text.stroke-102"),sQuery(id+"F4.wireOp",EDGE,"E10.sketch_text.stroke-103"),sQuery(id+"F4.wireOp",EDGE,"E10.sketch_text.stroke-104")])],"isStart":false});
            var Q117;
            Q117=makeQuery(id+"F5.opExtrude","SWEPT_FACE",FACE,{"disambiguationData":[OSD([sQuery(id+"F4.wireOp",EDGE,"E10.sketch_text.stroke-33")])]});
            var Q118;
            Q118=makeQuery(id+"F5.opExtrude","SWEPT_FACE",FACE,{"disambiguationData":[OSD([sQuery(id+"F4.wireOp",EDGE,"E10.sketch_text.stroke-93")])]});
            var Q119;
            Q119=makeQuery(id+"F5.opExtrude","SWEPT_FACE",FACE,{"disambiguationData":[OSD([sQuery(id+"F4.wireOp",EDGE,"E10.sketch_text.stroke-34")])]});
            var Q120;
            Q120=makeQuery(id+"F5.opExtrude","SWEPT_FACE",FACE,{"disambiguationData":[OSD([sQuery(id+"F4.wireOp",EDGE,"E10.sketch_text.stroke-152")])]});
            var Q121;
            Q121=makeQuery(id+"F5.opExtrude","SWEPT_FACE",FACE,{"disambiguationData":[OSD([sQuery(id+"F4.wireOp",EDGE,"E10.sketch_text.stroke-51")])]});
            var Q122;
            Q122=makeQuery(id+"F5.opExtrude","SWEPT_FACE",FACE,{"disambiguationData":[OSD([sQuery(id+"F4.wireOp",EDGE,"E10.sketch_text.stroke-6")])]});
            var Q123;
            Q123=makeQuery(id+"F5.opExtrude","SWEPT_FACE",FACE,{"disambiguationData":[OSD([sQuery(id+"F4.wireOp",EDGE,"E10.sketch_text.stroke-7")])]});
            var Q124;
            Q124=makeQuery(id+"F5.opExtrude","SWEPT_FACE",FACE,{"disambiguationData":[OSD([sQuery(id+"F4.wireOp",EDGE,"E10.sketch_text.stroke-156")])]});
            var Q125;
            Q125=makeQuery(id+"F5.opExtrude","SWEPT_FACE",FACE,{"disambiguationData":[OSD([sQuery(id+"F4.wireOp",EDGE,"E10.sketch_text.stroke-112")])]});
            var Q126;
            Q126=makeQuery(id+"F5.boolean.opBoolean","SPLIT",FACE,{"disambiguationData":[TD([makeQuery(id+"F5.opExtrude","SWEPT_FACE",FACE,{"disambiguationData":[OSD([sQuery(id+"F4.wireOp",EDGE,"E10.sketch_text.stroke-182")])]})])],"derivedFrom":makeQuery(id+"F1.opExtrude","CAP_FACE",FACE,{"disambiguationData":[OSD([sQuery(id+"F0.wireOp",EDGE,"E0.bottom"),sQuery(id+"F0.wireOp",EDGE,"E0.top"),sQuery(id+"F0.wireOp",EDGE,"E0.left"),sQuery(id+"F0.wireOp",EDGE,"E0.right"),sQuery(id+"F0.wireOp",EDGE,"E1"),sQuery(id+"F0.wireOp",EDGE,"E7.MirrorC"),sQuery(id+"F0.wireOp",EDGE,"E8.MirrorC"),sQuery(id+"F0.wireOp",EDGE,"E9.MirrorC")])],"isStart":true})});
            var Q127;
            Q127=makeQuery(id+"F5.opExtrude","SWEPT_FACE",FACE,{"disambiguationData":[OSD([sQuery(id+"F4.wireOp",EDGE,"E10.sketch_text.stroke-96")])]});
            var Q128;
            Q128=makeQuery(id+"F5.opExtrude","SWEPT_FACE",FACE,{"disambiguationData":[OSD([sQuery(id+"F4.wireOp",EDGE,"E10.sketch_text.stroke-114")])]});
            var Q129;
            Q129=makeQuery(id+"F5.opExtrude","SWEPT_FACE",FACE,{"disambiguationData":[OSD([sQuery(id+"F4.wireOp",EDGE,"E10.sketch_text.stroke-39")])]});
            var Q130;
            Q130=makeQuery(id+"F5.opExtrude","SWEPT_FACE",FACE,{"disambiguationData":[OSD([sQuery(id+"F4.wireOp",EDGE,"E10.sketch_text.stroke-13")])]});
            var Q131;
            Q131=makeQuery(id+"F5.opExtrude","SWEPT_FACE",FACE,{"disambiguationData":[OSD([sQuery(id+"F4.wireOp",EDGE,"E10.sketch_text.stroke-115")])]});
            var Q132;
            Q132=makeQuery(id+"F5.opExtrude","SWEPT_FACE",FACE,{"disambiguationData":[OSD([sQuery(id+"F4.wireOp",EDGE,"E10.sketch_text.stroke-56")])]});
            var Q133;
            Q133=makeQuery(id+"F5.opExtrude","SWEPT_FACE",FACE,{"disambiguationData":[OSD([sQuery(id+"F4.wireOp",EDGE,"E10.sketch_text.stroke-144")])]});
            var Q134;
            Q134=makeQuery(id+"F5.opExtrude","SWEPT_FACE",FACE,{"disambiguationData":[OSD([sQuery(id+"F4.wireOp",EDGE,"E10.sketch_text.stroke-190")])]});
            var Q135;
            Q135=makeQuery(id+"F5.opExtrude","SWEPT_FACE",FACE,{"disambiguationData":[OSD([sQuery(id+"F4.wireOp",EDGE,"E10.sketch_text.stroke-116")])]});
            var Q136;
            Q136=makeQuery(id+"F5.opExtrude","SWEPT_FACE",FACE,{"disambiguationData":[OSD([sQuery(id+"F4.wireOp",EDGE,"E10.sketch_text.stroke-41")])]});
            var Q137;
            Q137=makeQuery(id+"F5.opExtrude","SWEPT_FACE",FACE,{"disambiguationData":[OSD([sQuery(id+"F4.wireOp",EDGE,"E10.sketch_text.stroke-161")])]});
            var Q138;
            Q138=makeQuery(id+"F5.opExtrude","SWEPT_FACE",FACE,{"disambiguationData":[OSD([sQuery(id+"F4.wireOp",EDGE,"E10.sketch_text.stroke-146")])]});
            var Q139;
            Q139=makeQuery(id+"F5.opExtrude","SWEPT_FACE",FACE,{"disambiguationData":[OSD([sQuery(id+"F4.wireOp",EDGE,"E10.sketch_text.stroke-58")])]});
            var Q140;
            Q140=makeQuery(id+"F5.opExtrude","SWEPT_FACE",FACE,{"disambiguationData":[OSD([sQuery(id+"F4.wireOp",EDGE,"E10.sketch_text.stroke-105")])]});
            var Q141;
            Q141=makeQuery(id+"F5.opExtrude","SWEPT_FACE",FACE,{"disambiguationData":[OSD([sQuery(id+"F4.wireOp",EDGE,"E10.sketch_text.stroke-177")])]});
            var Q142;
            Q142=makeQuery(id+"F5.opExtrude","SWEPT_FACE",FACE,{"disambiguationData":[OSD([sQuery(id+"F4.wireOp",EDGE,"E10.sketch_text.stroke-77")])]});
            var Q143;
            Q143=makeQuery(id+"F5.opExtrude","SWEPT_FACE",FACE,{"disambiguationData":[OSD([sQuery(id+"F4.wireOp",EDGE,"E10.sketch_text.stroke-138")])]});
            var Q144;
            Q144=makeQuery(id+"F5.opExtrude","SWEPT_FACE",FACE,{"disambiguationData":[OSD([sQuery(id+"F4.wireOp",EDGE,"E10.sketch_text.stroke-111")])]});
            var Q145;
            Q145=makeQuery(id+"F5.opExtrude","SWEPT_FACE",FACE,{"disambiguationData":[OSD([sQuery(id+"F4.wireOp",EDGE,"E10.sketch_text.stroke-53")])]});
            var Q146;
            Q146=makeQuery(id+"F5.opExtrude","SWEPT_FACE",FACE,{"disambiguationData":[OSD([sQuery(id+"F4.wireOp",EDGE,"E10.sketch_text.stroke-141")])]});
            var Q147;
            Q147=makeQuery(id+"F5.opExtrude","SWEPT_FACE",FACE,{"disambiguationData":[OSD([sQuery(id+"F4.wireOp",EDGE,"E10.sketch_text.stroke-157")])]});
            var Q148;
            Q148=makeQuery(id+"F5.opExtrude","SWEPT_FACE",FACE,{"disambiguationData":[OSD([sQuery(id+"F4.wireOp",EDGE,"E10.sketch_text.stroke-64")])]});
            var Q149;
            Q149=makeQuery(id+"F5.boolean.opBoolean","SPLIT",FACE,{"disambiguationData":[TD([makeQuery(id+"F5.opExtrude","SWEPT_FACE",FACE,{"disambiguationData":[OSD([sQuery(id+"F4.wireOp",EDGE,"E10.sketch_text.stroke-53")])]})])],"derivedFrom":makeQuery(id+"F1.opExtrude","CAP_FACE",FACE,{"disambiguationData":[OSD([sQuery(id+"F0.wireOp",EDGE,"E0.bottom"),sQuery(id+"F0.wireOp",EDGE,"E0.top"),sQuery(id+"F0.wireOp",EDGE,"E0.left"),sQuery(id+"F0.wireOp",EDGE,"E0.right"),sQuery(id+"F0.wireOp",EDGE,"E1"),sQuery(id+"F0.wireOp",EDGE,"E7.MirrorC"),sQuery(id+"F0.wireOp",EDGE,"E8.MirrorC"),sQuery(id+"F0.wireOp",EDGE,"E9.MirrorC")])],"isStart":true})});
            var Q150;
            Q150=makeQuery(id+"F5.opExtrude","SWEPT_FACE",FACE,{"disambiguationData":[OSD([sQuery(id+"F4.wireOp",EDGE,"E10.sketch_text.stroke-36")])]});
            var Q151;
            Q151=makeQuery(id+"F5.opExtrude","SWEPT_FACE",FACE,{"disambiguationData":[OSD([sQuery(id+"F4.wireOp",EDGE,"E10.sketch_text.stroke-22")])]});
            var Q152;
            Q152=makeQuery(id+"F5.boolean.opBoolean","SPLIT",FACE,{"disambiguationData":[TD([makeQuery(id+"F5.opExtrude","SWEPT_FACE",FACE,{"disambiguationData":[OSD([sQuery(id+"F4.wireOp",EDGE,"E10.sketch_text.stroke-119")])]})])],"derivedFrom":makeQuery(id+"F1.opExtrude","CAP_FACE",FACE,{"disambiguationData":[OSD([sQuery(id+"F0.wireOp",EDGE,"E0.bottom"),sQuery(id+"F0.wireOp",EDGE,"E0.top"),sQuery(id+"F0.wireOp",EDGE,"E0.left"),sQuery(id+"F0.wireOp",EDGE,"E0.right"),sQuery(id+"F0.wireOp",EDGE,"E1"),sQuery(id+"F0.wireOp",EDGE,"E7.MirrorC"),sQuery(id+"F0.wireOp",EDGE,"E8.MirrorC"),sQuery(id+"F0.wireOp",EDGE,"E9.MirrorC")])],"isStart":true})});
            var Q153;
            Q153=makeQuery(id+"F5.boolean.opBoolean","SPLIT",FACE,{"disambiguationData":[TD([makeQuery(id+"F5.opExtrude","SWEPT_FACE",FACE,{"disambiguationData":[OSD([sQuery(id+"F4.wireOp",EDGE,"E10.sketch_text.stroke-158")])]})])],"derivedFrom":makeQuery(id+"F1.opExtrude","CAP_FACE",FACE,{"disambiguationData":[OSD([sQuery(id+"F0.wireOp",EDGE,"E0.bottom"),sQuery(id+"F0.wireOp",EDGE,"E0.top"),sQuery(id+"F0.wireOp",EDGE,"E0.left"),sQuery(id+"F0.wireOp",EDGE,"E0.right"),sQuery(id+"F0.wireOp",EDGE,"E1"),sQuery(id+"F0.wireOp",EDGE,"E7.MirrorC"),sQuery(id+"F0.wireOp",EDGE,"E8.MirrorC"),sQuery(id+"F0.wireOp",EDGE,"E9.MirrorC")])],"isStart":true})});
            var Q154;
            Q154=makeQuery(id+"F5.opExtrude","SWEPT_FACE",FACE,{"disambiguationData":[OSD([sQuery(id+"F4.wireOp",EDGE,"E10.sketch_text.stroke-9")])]});
            var Q155;
            Q155=makeQuery(id+"F5.opExtrude","SWEPT_FACE",FACE,{"disambiguationData":[OSD([sQuery(id+"F4.wireOp",EDGE,"E10.sketch_text.stroke-167")])]});
            var Q156;
            Q156=makeQuery(id+"F5.opExtrude","SWEPT_FACE",FACE,{"disambiguationData":[OSD([sQuery(id+"F4.wireOp",EDGE,"E10.sketch_text.stroke-95")])]});
            var Q157;
            Q157=makeQuery(id+"F5.opExtrude","SWEPT_FACE",FACE,{"disambiguationData":[OSD([sQuery(id+"F4.wireOp",EDGE,"E10.sketch_text.stroke-184")])]});
            var Q158;
            Q158=makeQuery(id+"F5.opExtrude","SWEPT_FACE",FACE,{"disambiguationData":[OSD([sQuery(id+"F4.wireOp",EDGE,"E10.sketch_text.stroke-84")])]});
            var Q159;
            Q159=makeQuery(id+"F5.opExtrude","SWEPT_FACE",FACE,{"disambiguationData":[OSD([sQuery(id+"F4.wireOp",EDGE,"E10.sketch_text.stroke-68")])]});
            var Q160;
            Q160=makeQuery(id+"F5.opExtrude","SWEPT_FACE",FACE,{"disambiguationData":[OSD([sQuery(id+"F4.wireOp",EDGE,"E10.sketch_text.stroke-143")])]});
            var Q161;
            Q161=makeQuery(id+"F5.opExtrude","SWEPT_FACE",FACE,{"disambiguationData":[OSD([sQuery(id+"F4.wireOp",EDGE,"E10.sketch_text.stroke-189")])]});
            var Q162;
            Q162=makeQuery(id+"F5.opExtrude","CAP_FACE",FACE,{"disambiguationData":[OSD([sQuery(id+"F4.wireOp",EDGE,"E10.sketch_text.stroke-13"),sQuery(id+"F4.wireOp",EDGE,"E10.sketch_text.stroke-14"),sQuery(id+"F4.wireOp",EDGE,"E10.sketch_text.stroke-15"),sQuery(id+"F4.wireOp",EDGE,"E10.sketch_text.stroke-16"),sQuery(id+"F4.wireOp",EDGE,"E10.sketch_text.stroke-17"),sQuery(id+"F4.wireOp",EDGE,"E10.sketch_text.stroke-18"),sQuery(id+"F4.wireOp",EDGE,"E10.sketch_text.stroke-19"),sQuery(id+"F4.wireOp",EDGE,"E10.sketch_text.stroke-20")])],"isStart":false});
            var Q163;
            Q163=makeQuery(id+"F5.opExtrude","SWEPT_FACE",FACE,{"disambiguationData":[OSD([sQuery(id+"F4.wireOp",EDGE,"E10.sketch_text.stroke-57")])]});
            var Q164;
            Q164=makeQuery(id+"F5.opExtrude","SWEPT_FACE",FACE,{"disambiguationData":[OSD([sQuery(id+"F4.wireOp",EDGE,"E10.sketch_text.stroke-29")])]});
            var Q165;
            Q165=makeQuery(id+"F5.opExtrude","SWEPT_FACE",FACE,{"disambiguationData":[OSD([sQuery(id+"F4.wireOp",EDGE,"E10.sketch_text.stroke-60")])]});
            var Q166;
            Q166=makeQuery(id+"F5.opExtrude","SWEPT_FACE",FACE,{"disambiguationData":[OSD([sQuery(id+"F4.wireOp",EDGE,"E10.sketch_text.stroke-148")])]});
            var Q167;
            Q167=makeQuery(id+"F5.opExtrude","SWEPT_FACE",FACE,{"disambiguationData":[OSD([sQuery(id+"F4.wireOp",EDGE,"E10.sketch_text.stroke-75")])]});
            var Q168;
            Q168=makeQuery(id+"F5.opExtrude","SWEPT_FACE",FACE,{"disambiguationData":[OSD([sQuery(id+"F4.wireOp",EDGE,"E10.sketch_text.stroke-91")])]});
            var Q169;
            Q169=makeQuery(id+"F5.opExtrude","SWEPT_FACE",FACE,{"disambiguationData":[OSD([sQuery(id+"F4.wireOp",EDGE,"E10.sketch_text.stroke-78")])]});
            var Q170;
            Q170=makeQuery(id+"F5.opExtrude","SWEPT_FACE",FACE,{"disambiguationData":[OSD([sQuery(id+"F4.wireOp",EDGE,"E10.sketch_text.stroke-62")])]});
            var Q171;
            Q171=makeQuery(id+"F5.opExtrude","SWEPT_FACE",FACE,{"disambiguationData":[OSD([sQuery(id+"F4.wireOp",EDGE,"E10.sketch_text.stroke-182")])]});
            var Q172;
            Q172=makeQuery(id+"F5.opExtrude","SWEPT_FACE",FACE,{"disambiguationData":[OSD([sQuery(id+"F4.wireOp",EDGE,"E10.sketch_text.stroke-11")])]});
            var Q173;
            Q173=makeQuery(id+"F5.opExtrude","SWEPT_FACE",FACE,{"disambiguationData":[OSD([sQuery(id+"F4.wireOp",EDGE,"E10.sketch_text.stroke-97")])]});
            var Q174;
            Q174=makeQuery(id+"F5.opExtrude","SWEPT_FACE",FACE,{"disambiguationData":[OSD([sQuery(id+"F4.wireOp",EDGE,"E10.sketch_text.stroke-23")])]});
            var Q175;
            Q175=makeQuery(id+"F5.opExtrude","SWEPT_FACE",FACE,{"disambiguationData":[OSD([sQuery(id+"F4.wireOp",EDGE,"E10.sketch_text.stroke-80")])]});
            var Q176;
            Q176=makeQuery(id+"F5.boolean.opBoolean","SPLIT",FACE,{"disambiguationData":[TD([makeQuery(id+"F5.opExtrude","SWEPT_FACE",FACE,{"disambiguationData":[OSD([sQuery(id+"F4.wireOp",EDGE,"E10.sketch_text.stroke-99")])]})])],"derivedFrom":makeQuery(id+"F1.opExtrude","CAP_FACE",FACE,{"disambiguationData":[OSD([sQuery(id+"F0.wireOp",EDGE,"E0.bottom"),sQuery(id+"F0.wireOp",EDGE,"E0.top"),sQuery(id+"F0.wireOp",EDGE,"E0.left"),sQuery(id+"F0.wireOp",EDGE,"E0.right"),sQuery(id+"F0.wireOp",EDGE,"E1"),sQuery(id+"F0.wireOp",EDGE,"E7.MirrorC"),sQuery(id+"F0.wireOp",EDGE,"E8.MirrorC"),sQuery(id+"F0.wireOp",EDGE,"E9.MirrorC")])],"isStart":true})});
            var Q177;
            Q177=makeQuery(id+"F5.opExtrude","SWEPT_FACE",FACE,{"disambiguationData":[OSD([sQuery(id+"F4.wireOp",EDGE,"E10.sketch_text.stroke-168")])]});
            var Q178;
            Q178=makeQuery(id+"F5.opExtrude","SWEPT_FACE",FACE,{"disambiguationData":[OSD([sQuery(id+"F4.wireOp",EDGE,"E10.sketch_text.stroke-188")])]});
            var Q179;
            Q179=makeQuery(id+"F5.opExtrude","SWEPT_FACE",FACE,{"disambiguationData":[OSD([sQuery(id+"F4.wireOp",EDGE,"E10.sketch_text.stroke-129")])]});
            var Q180;
            Q180=makeQuery(id+"F5.opExtrude","SWEPT_FACE",FACE,{"disambiguationData":[OSD([sQuery(id+"F4.wireOp",EDGE,"E10.sketch_text.stroke-27")])]});
            var Q181;
            Q181=makeQuery(id+"F5.opExtrude","SWEPT_FACE",FACE,{"disambiguationData":[OSD([sQuery(id+"F4.wireOp",EDGE,"E10.sketch_text.stroke-175")])]});
            var Q182;
            Q182=makeQuery(id+"F5.opExtrude","SWEPT_FACE",FACE,{"disambiguationData":[OSD([sQuery(id+"F4.wireOp",EDGE,"E10.sketch_text.stroke-42")])]});
            var Q183;
            Q183=makeQuery(id+"F5.opExtrude","SWEPT_FACE",FACE,{"disambiguationData":[OSD([sQuery(id+"F4.wireOp",EDGE,"E10.sketch_text.stroke-118")])]});
            var Q184;
            Q184=makeQuery(id+"F5.opExtrude","SWEPT_FACE",FACE,{"disambiguationData":[OSD([sQuery(id+"F4.wireOp",EDGE,"E10.sketch_text.stroke-151")])]});
            var Q185;
            Q185=makeQuery(id+"F5.opExtrude","SWEPT_FACE",FACE,{"disambiguationData":[OSD([sQuery(id+"F4.wireOp",EDGE,"E10.sketch_text.stroke-137")])]});
            var Q186;
            Q186=makeQuery(id+"F5.opExtrude","SWEPT_FACE",FACE,{"disambiguationData":[OSD([sQuery(id+"F4.wireOp",EDGE,"E10.sketch_text.stroke-83")])]});
            var Q187;
            Q187=makeQuery(id+"F5.boolean.opBoolean","SPLIT",FACE,{"disambiguationData":[TD([makeQuery(id+"F5.opExtrude","SWEPT_FACE",FACE,{"disambiguationData":[OSD([sQuery(id+"F4.wireOp",EDGE,"E10.sketch_text.stroke-90")])]})])],"derivedFrom":makeQuery(id+"F1.opExtrude","CAP_FACE",FACE,{"disambiguationData":[OSD([sQuery(id+"F0.wireOp",EDGE,"E0.bottom"),sQuery(id+"F0.wireOp",EDGE,"E0.top"),sQuery(id+"F0.wireOp",EDGE,"E0.left"),sQuery(id+"F0.wireOp",EDGE,"E0.right"),sQuery(id+"F0.wireOp",EDGE,"E1"),sQuery(id+"F0.wireOp",EDGE,"E7.MirrorC"),sQuery(id+"F0.wireOp",EDGE,"E8.MirrorC"),sQuery(id+"F0.wireOp",EDGE,"E9.MirrorC")])],"isStart":true})});
            var Q188;
            Q188=makeQuery(id+"F5.opExtrude","SWEPT_FACE",FACE,{"disambiguationData":[OSD([sQuery(id+"F4.wireOp",EDGE,"E10.sketch_text.stroke-139")])]});
            var Q189;
            Q189=makeQuery(id+"F5.opExtrude","SWEPT_FACE",FACE,{"disambiguationData":[OSD([sQuery(id+"F4.wireOp",EDGE,"E10.sketch_text.stroke-70")])]});
            var Q190;
            Q190=makeQuery(id+"F5.opExtrude","SWEPT_FACE",FACE,{"disambiguationData":[OSD([sQuery(id+"F4.wireOp",EDGE,"E10.sketch_text.stroke-160")])]});
            var Q191;
            Q191=makeQuery(id+"F5.opExtrude","SWEPT_FACE",FACE,{"disambiguationData":[OSD([sQuery(id+"F4.wireOp",EDGE,"E10.sketch_text.stroke-71")])]});
            var Q192;
            Q192=makeQuery(id+"F5.opExtrude","SWEPT_FACE",FACE,{"disambiguationData":[OSD([sQuery(id+"F4.wireOp",EDGE,"E10.sketch_text.stroke-117")])]});
            var Q193;
            Q193=makeQuery(id+"F5.opExtrude","SWEPT_FACE",FACE,{"disambiguationData":[OSD([sQuery(id+"F4.wireOp",EDGE,"E10.sketch_text.stroke-147")])]});
            var Q194;
            Q194=makeQuery(id+"F5.opExtrude","SWEPT_FACE",FACE,{"disambiguationData":[OSD([sQuery(id+"F4.wireOp",EDGE,"E10.sketch_text.stroke-164")])]});
            var Q195;
            Q195=makeQuery(id+"F5.opExtrude","SWEPT_FACE",FACE,{"disambiguationData":[OSD([sQuery(id+"F4.wireOp",EDGE,"E10.sketch_text.stroke-61")])]});
            var Q196;
            Q196=makeQuery(id+"F5.opExtrude","SWEPT_FACE",FACE,{"disambiguationData":[OSD([sQuery(id+"F4.wireOp",EDGE,"E10.sketch_text.stroke-19")])]});
            var Q197;
            Q197=makeQuery(id+"F5.opExtrude","SWEPT_FACE",FACE,{"disambiguationData":[OSD([sQuery(id+"F4.wireOp",EDGE,"E10.sketch_text.stroke-35")])]});
            var Q198;
            Q198=makeQuery(id+"F5.opExtrude","SWEPT_FACE",FACE,{"disambiguationData":[OSD([sQuery(id+"F4.wireOp",EDGE,"E10.sketch_text.stroke-140")])]});
            var Q199;
            Q199=makeQuery(id+"F5.opExtrude","SWEPT_FACE",FACE,{"disambiguationData":[OSD([sQuery(id+"F4.wireOp",EDGE,"E10.sketch_text.stroke-20")])]});
            var Q200;
            Q200=makeQuery(id+"F5.opExtrude","SWEPT_FACE",FACE,{"disambiguationData":[OSD([sQuery(id+"F4.wireOp",EDGE,"E10.sketch_text.stroke-16")])]});
            var Q201;
            Q201=makeQuery(id+"F5.opExtrude","SWEPT_FACE",FACE,{"disambiguationData":[OSD([sQuery(id+"F4.wireOp",EDGE,"E10.sketch_text.stroke-18")])]});
            var Q202;
            Q202=makeQuery(id+"F5.opExtrude","SWEPT_FACE",FACE,{"disambiguationData":[OSD([sQuery(id+"F4.wireOp",EDGE,"E10.sketch_text.stroke-17")])]});
            var Q203;
            Q203=qCreatedBy(makeId("Right.planeOp"),FACE);
            mirror(context, id + "F6", {"operationType" : NewBodyOperationType.ADD, "entities" : qUnion([Q0]), "faces" : qUnion([Q1, Q2, Q3, Q4, Q5, Q6, Q7, Q8, Q9, Q10, Q11, Q12, Q13, Q14, Q15, Q16, Q17, Q18, Q19, Q20, Q21, Q22, Q23, Q24, Q25, Q26, Q27, Q28, Q29, Q30, Q31, Q32, Q33, Q34, Q35, Q36, Q37, Q38, Q39, Q40, Q41, Q42, Q43, Q44, Q45, Q46, Q47, Q48, Q49, Q50, Q51, Q52, Q53, Q54, Q55, Q56, Q57, Q58, Q59, Q60, Q61, Q62, Q63, Q64, Q65, Q66, Q67, Q68, Q69, Q70, Q71, Q72, Q73, Q74, Q75, Q76, Q77, Q78, Q79, Q80, Q81, Q82, Q83, Q84, Q85, Q86, Q87, Q88, Q89, Q90, Q91, Q92, Q93, Q94, Q95, Q96, Q97, Q98, Q99, Q100, Q101, Q102, Q103, Q104, Q105, Q106, Q107, Q108, Q109, Q110, Q111, Q112, Q113, Q114, Q115, Q116, Q117, Q118, Q119, Q120, Q121, Q122, Q123, Q124, Q125, Q126, Q127, Q128, Q129, Q130, Q131, Q132, Q133, Q134, Q135, Q136, Q137, Q138, Q139, Q140, Q141, Q142, Q143, Q144, Q145, Q146, Q147, Q148, Q149, Q150, Q151, Q152, Q153, Q154, Q155, Q156, Q157, Q158, Q159, Q160, Q161, Q162, Q163, Q164, Q165, Q166, Q167, Q168, Q169, Q170, Q171, Q172, Q173, Q174, Q175, Q176, Q177, Q178, Q179, Q180, Q181, Q182, Q183, Q184, Q185, Q186, Q187, Q188, Q189, Q190, Q191, Q192, Q193, Q194, Q195, Q196, Q197, Q198, Q199, Q200, Q201, Q202]), "mirrorPlane" : qUnion([Q203])});
        }
    });
